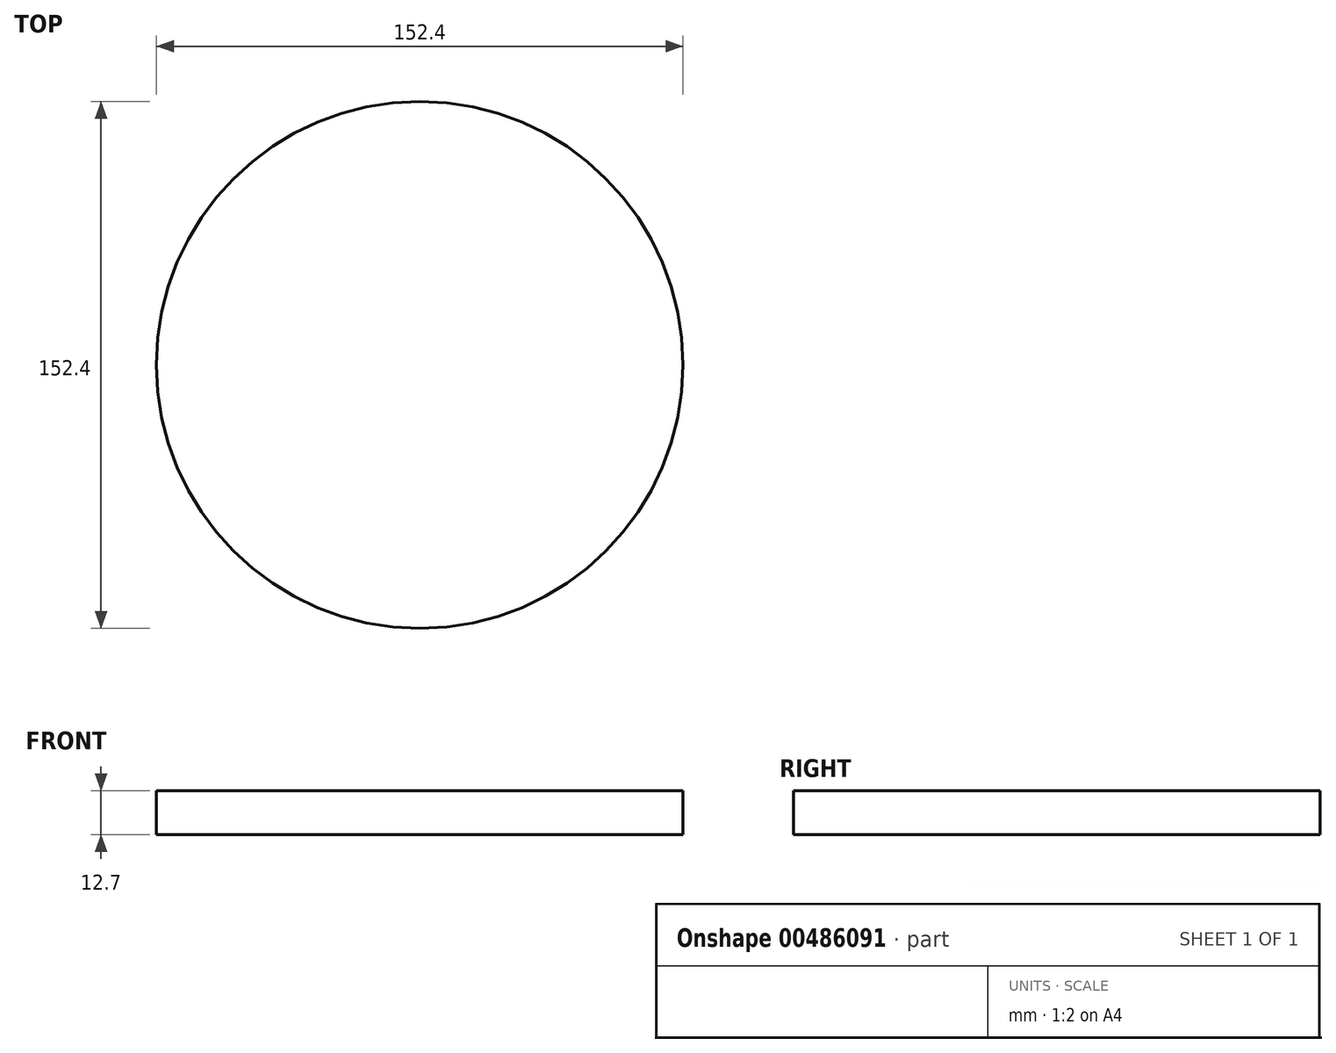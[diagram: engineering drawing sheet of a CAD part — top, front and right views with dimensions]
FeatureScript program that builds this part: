
annotation { "Feature Type Name" : "Feature", "Feature Type Description" : "" }
export const myFeature = defineFeature(function(context is Context, id is Id, definition is map)
    precondition{}
    {
        {
            var Q0;
            Q0=qCreatedBy(makeId("Top.planeOp"),FACE);
            var sketch = newSketch(context, id + "F0", { "sketchPlane" : qUnion([Q0])});
            skCircle(sketch, "E0", {"center": v(0, 0) * mm, "radius": 76.2 * mm});
            skSolve(sketch);
        }
        {
            var Q0;
            Q0 = qSketchRegion(id + "F0", true);
            extrude(context, id + "F1", {"entities" : qUnion([Q0]), "depth" : 12.7 * mm});
        }
    });
